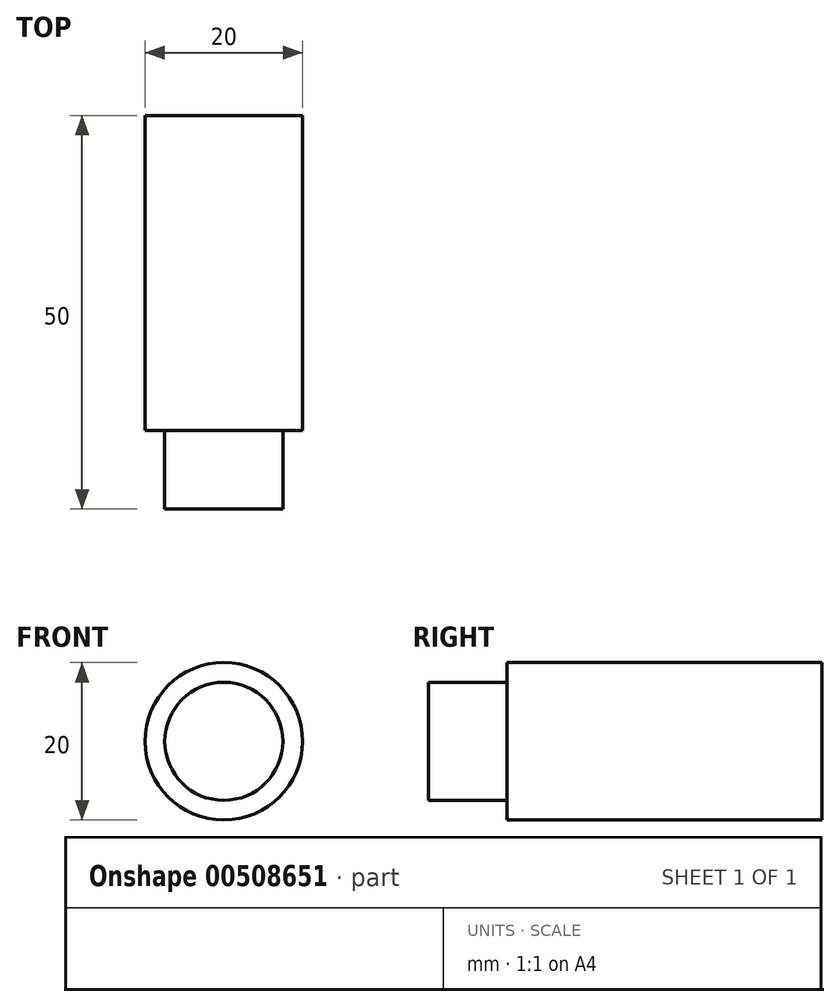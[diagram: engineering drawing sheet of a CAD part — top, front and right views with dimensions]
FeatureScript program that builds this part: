
annotation { "Feature Type Name" : "Feature", "Feature Type Description" : "" }
export const myFeature = defineFeature(function(context is Context, id is Id, definition is map)
    precondition{}
    {
        {
            var Q0;
            Q0=qCreatedBy(makeId("Front.planeOp"),FACE);
            var sketch = newSketch(context, id + "F0", { "sketchPlane" : qUnion([Q0])});
            skCircle(sketch, "E0", {"center": v(0, 0) * mm, "radius": 10 * mm});
            skSolve(sketch);
        }
        {
            var Q0;
            Q0 = qSketchRegion(id + "F0", true);
            extrude(context, id + "F1", {"entities" : qUnion([Q0]), "depth" : 50 * mm});
        }
        {
            var Q0;
            Q0=makeQuery(id+"F1.opExtrude","CAP_FACE",FACE,{"disambiguationData":[OSD([sQuery(id+"F0.wireOp",EDGE,"E0")])],"isStart":false});
            var sketch = newSketch(context, id + "F2", { "sketchPlane" : qUnion([Q0])});
            skCircle(sketch, "E1", {"center": v(0, 0) * mm, "radius": 7.5 * mm});
            skSolve(sketch);
        }
        {
            var Q0;
            Q0=makeQuery(id+"F2.imprint","IMPRINT",FACE,{"disambiguationData":[TD([[makeQuery(id+"F2.imprint","IMPRINT",EDGE,{"derivedFrom":sQuery(id+"F2.wireOp",EDGE,"E1")}),-1.0]])]});
            extrude(context, id + "F3", {"entities" : qUnion([Q0]), "operationType" : NewBodyOperationType.REMOVE, "oppositeDirection" : true, "depth" : 10 * mm, "offsetDistance" : 25 * mm});
        }
    });
